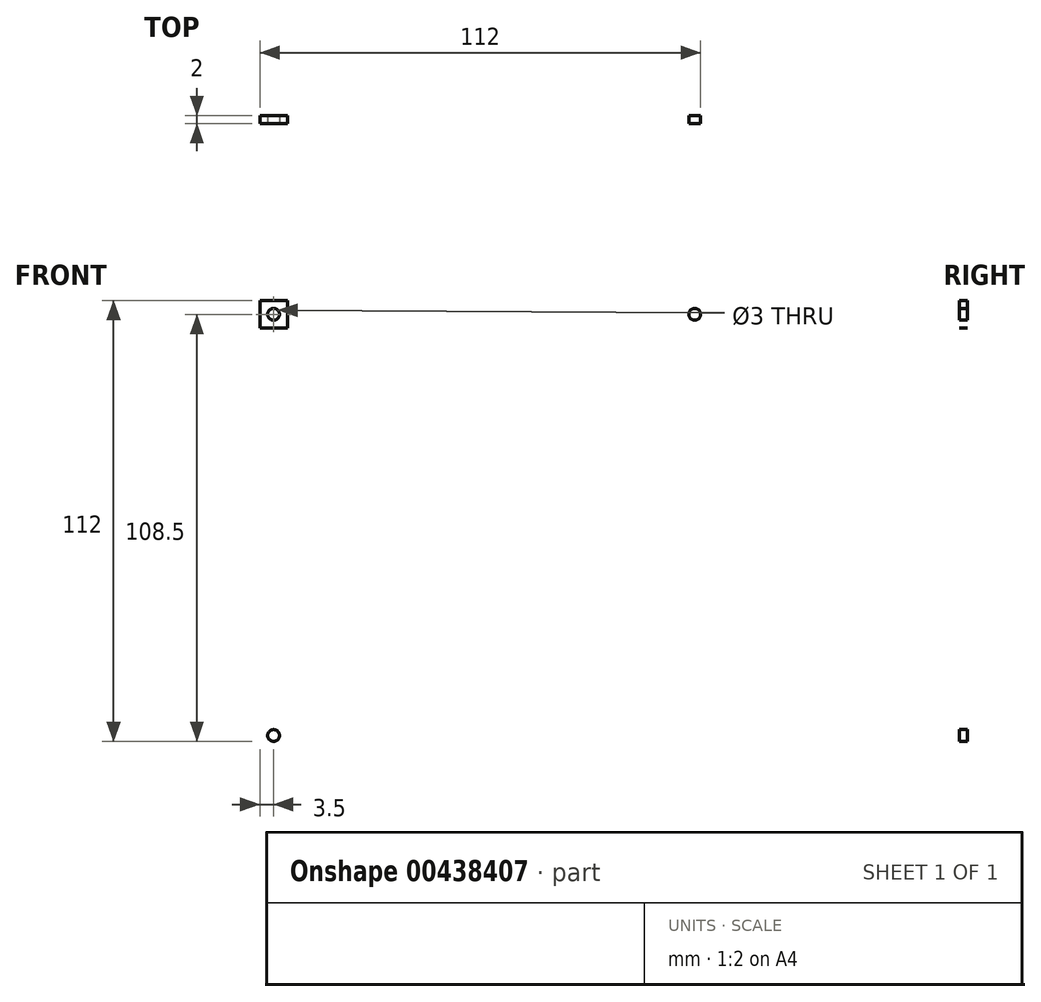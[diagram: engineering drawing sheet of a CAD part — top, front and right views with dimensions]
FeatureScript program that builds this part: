
annotation { "Feature Type Name" : "Feature", "Feature Type Description" : "" }
export const myFeature = defineFeature(function(context is Context, id is Id, definition is map)
    precondition{}
    {
        {
            var Q0;
            Q0=qCreatedBy(makeId("Front.planeOp"),FACE);
            var sketch = newSketch(context, id + "F0", { "sketchPlane" : qUnion([Q0])});
            skLineSegment(sketch, "E0.bottom", {"start": v(57, 57) * mm, "end": v(-57, 57) * mm});
            skLineSegment(sketch, "E0.top", {"start": v(57, -57) * mm, "end": v(-57, -57) * mm});
            skLineSegment(sketch, "E0.left", {"start": v(57, 57) * mm, "end": v(57, -57) * mm});
            skLineSegment(sketch, "E0.right", {"start": v(-57, 57) * mm, "end": v(-57, -57) * mm});
            skPoint(sketch, "E0.middle", {"position": v(0, 0) * mm});
            skSolve(sketch);
        }
        {
            var Q0;
            Q0 = qSketchRegion(id + "F0", true);
            extrude(context, id + "F1", {"entities" : qUnion([Q0]), "depth" : 2 * mm});
        }
        {
            var Q0;
            Q0=makeQuery(id+"F1.opExtrude","CAP_FACE",FACE,{"disambiguationData":[OSD([sQuery(id+"F0.wireOp",EDGE,"E0.bottom"),sQuery(id+"F0.wireOp",EDGE,"E0.top"),sQuery(id+"F0.wireOp",EDGE,"E0.left"),sQuery(id+"F0.wireOp",EDGE,"E0.right")])],"isStart":false});
            var sketch = newSketch(context, id + "F2", { "sketchPlane" : qUnion([Q0])});
            skLineSegment(sketch, "E1.bottom", {"start": v(-57, 57) * mm, "end": v(-50, 57) * mm});
            skLineSegment(sketch, "E1.top", {"start": v(-57, 50) * mm, "end": v(-50, 50) * mm});
            skLineSegment(sketch, "E1.left", {"start": v(-57, 57) * mm, "end": v(-57, 50) * mm});
            skLineSegment(sketch, "E1.right", {"start": v(-50, 57) * mm, "end": v(-50, 50) * mm});
            skLineSegment(sketch, "E2", {"start": v(-50, 50) * mm, "end": v(-57, 57) * mm, "construction": true});
            skCircle(sketch, "E3", {"center": v(-53.5, 53.5) * mm, "radius": 1.5 * mm});
            skCircle(sketch, "E4.MirrorC", {"center": v(53.5, 53.5) * mm, "radius": 1.5 * mm});
            skCircle(sketch, "E5.MirrorC", {"center": v(53.5, -53.5) * mm, "radius": 1.5 * mm});
            skCircle(sketch, "E6.MirrorC", {"center": v(-53.5, -53.5) * mm, "radius": 1.5 * mm});
            skSolve(sketch);
        }
        {
            var Q0;
            Q0=makeQuery(id+"F2.imprint","IMPRINT",FACE,{"disambiguationData":[TD([[makeQuery(id+"F2.imprint","IMPRINT",EDGE,{"derivedFrom":sQuery(id+"F2.wireOp",EDGE,"E3")}),1.0]])]});
            extrude(context, id + "F3", {"entities" : qUnion([Q0]), "operationType" : NewBodyOperationType.REMOVE, "endBound" : BoundingType.THROUGH_ALL, "oppositeDirection" : true, "depth" : 25 * mm});
        }
        {
            var Q0;
            Q0=makeQuery(id+"F2.imprint","IMPRINT",FACE,{"disambiguationData":[TD([[makeQuery(id+"F2.imprint","IMPRINT",EDGE,{"derivedFrom":sQuery(id+"F2.wireOp",EDGE,"E3")}),1.0]])]});
            var Q1;
            Q1=makeQuery(id+"F2.imprint","IMPRINT",FACE,{"disambiguationData":[TD([[makeQuery(id+"F2.imprint","IMPRINT",EDGE,{"derivedFrom":sQuery(id+"F2.wireOp",EDGE,"E4.MirrorC")}),-1.0]])]});
            var Q2;
            Q2=makeQuery(id+"F2.imprint","IMPRINT",FACE,{"disambiguationData":[TD([[makeQuery(id+"F2.imprint","IMPRINT",EDGE,{"derivedFrom":sQuery(id+"F2.wireOp",EDGE,"E5.MirrorC")}),1.0]])]});
            var Q3;
            Q3=makeQuery(id+"F2.imprint","IMPRINT",FACE,{"disambiguationData":[TD([[makeQuery(id+"F2.imprint","IMPRINT",EDGE,{"derivedFrom":sQuery(id+"F2.wireOp",EDGE,"E6.MirrorC")}),-1.0]])]});
            extrude(context, id + "F4", {"entities" : qUnion([Q0, Q1, Q2, Q3]), "operationType" : NewBodyOperationType.REMOVE, "endBound" : BoundingType.THROUGH_ALL, "oppositeDirection" : true, "depth" : 25 * mm});
        }
    });
